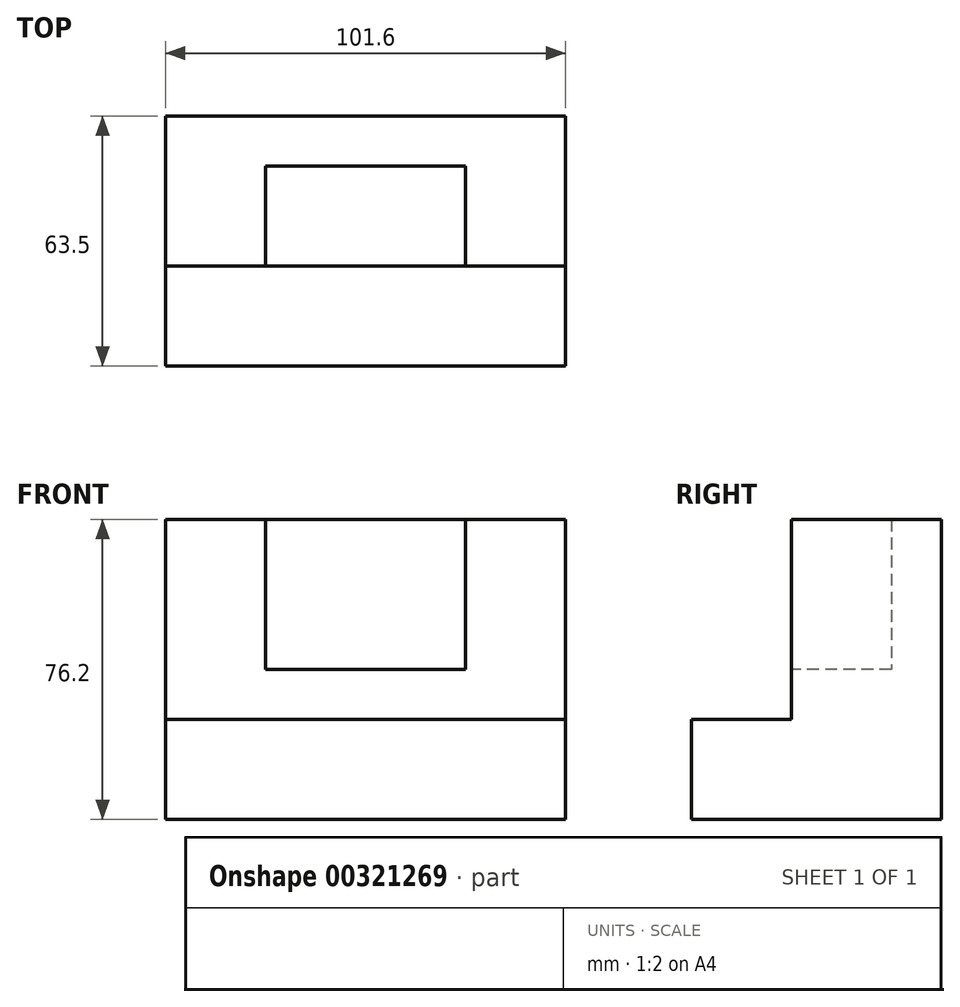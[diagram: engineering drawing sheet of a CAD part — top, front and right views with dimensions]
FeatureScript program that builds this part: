
annotation { "Feature Type Name" : "Feature", "Feature Type Description" : "" }
export const myFeature = defineFeature(function(context is Context, id is Id, definition is map)
    precondition{}
    {
        {
            var Q0;
            Q0=qCreatedBy(makeId("Right.planeOp"),FACE);
            var sketch = newSketch(context, id + "F0", { "sketchPlane" : qUnion([Q0])});
            skLineSegment(sketch, "E0", {"start": v(57.9, 28.7) * mm, "end": v(57.9, -47.5) * mm});
            skLineSegment(sketch, "E1", {"start": v(57.9, 28.7) * mm, "end": v(19.8, 28.7) * mm});
            skLineSegment(sketch, "E2", {"start": v(19.8, 28.7) * mm, "end": v(19.8, -22.1) * mm});
            skLineSegment(sketch, "E3", {"start": v(19.8, -22.1) * mm, "end": v(-5.6, -22.1) * mm});
            skLineSegment(sketch, "E4", {"start": v(-5.6, -22.1) * mm, "end": v(-5.6, -47.5) * mm});
            skLineSegment(sketch, "E5", {"start": v(-5.6, -47.5) * mm, "end": v(57.9, -47.5) * mm});
            skSolve(sketch);
        }
        {
            var Q0;
            Q0 = qSketchRegion(id + "F0", true);
            extrude(context, id + "F1", {"entities" : qUnion([Q0]), "oppositeDirection" : true, "depth" : 101.6 * mm});
        }
        {
            var Q0;
            Q0=makeQuery(id+"F1.opExtrude","SWEPT_FACE",FACE,{"disambiguationData":[OSD([sQuery(id+"F0.wireOp",EDGE,"E2")])]});
            var sketch = newSketch(context, id + "F2", { "sketchPlane" : qUnion([Q0])});
            skLineSegment(sketch, "E6", {"start": v(-101.6, 28.7) * mm, "end": v(-76.2, 28.7) * mm});
            skLineSegment(sketch, "E7", {"start": v(-76.2, 28.7) * mm, "end": v(-76.2, -9.4) * mm});
            skLineSegment(sketch, "E8", {"start": v(-76.2, -9.4) * mm, "end": v(-25.4, -9.4) * mm});
            skLineSegment(sketch, "E9", {"start": v(-25.4, -9.4) * mm, "end": v(-25.4, 28.7) * mm});
            skLineSegment(sketch, "E10", {"start": v(-25.4, 28.7) * mm, "end": v(0, 28.7) * mm});
            skSolve(sketch);
        }
        {
            var Q0;
            {var subQ0=sQuery(id+"F2.wireOp",EDGE,"E7");Q0=makeQuery(id+"F2.imprint","IMPRINT",FACE,{"disambiguationData":[TD([[makeQuery(id+"F2.imprint","IMPRINT",EDGE,{"derivedFrom":subQ0}),1.0]])]});}
            extrude(context, id + "F3", {"entities" : qUnion([Q0]), "operationType" : NewBodyOperationType.REMOVE, "oppositeDirection" : true, "depth" : 25.4 * mm});
        }
    });
